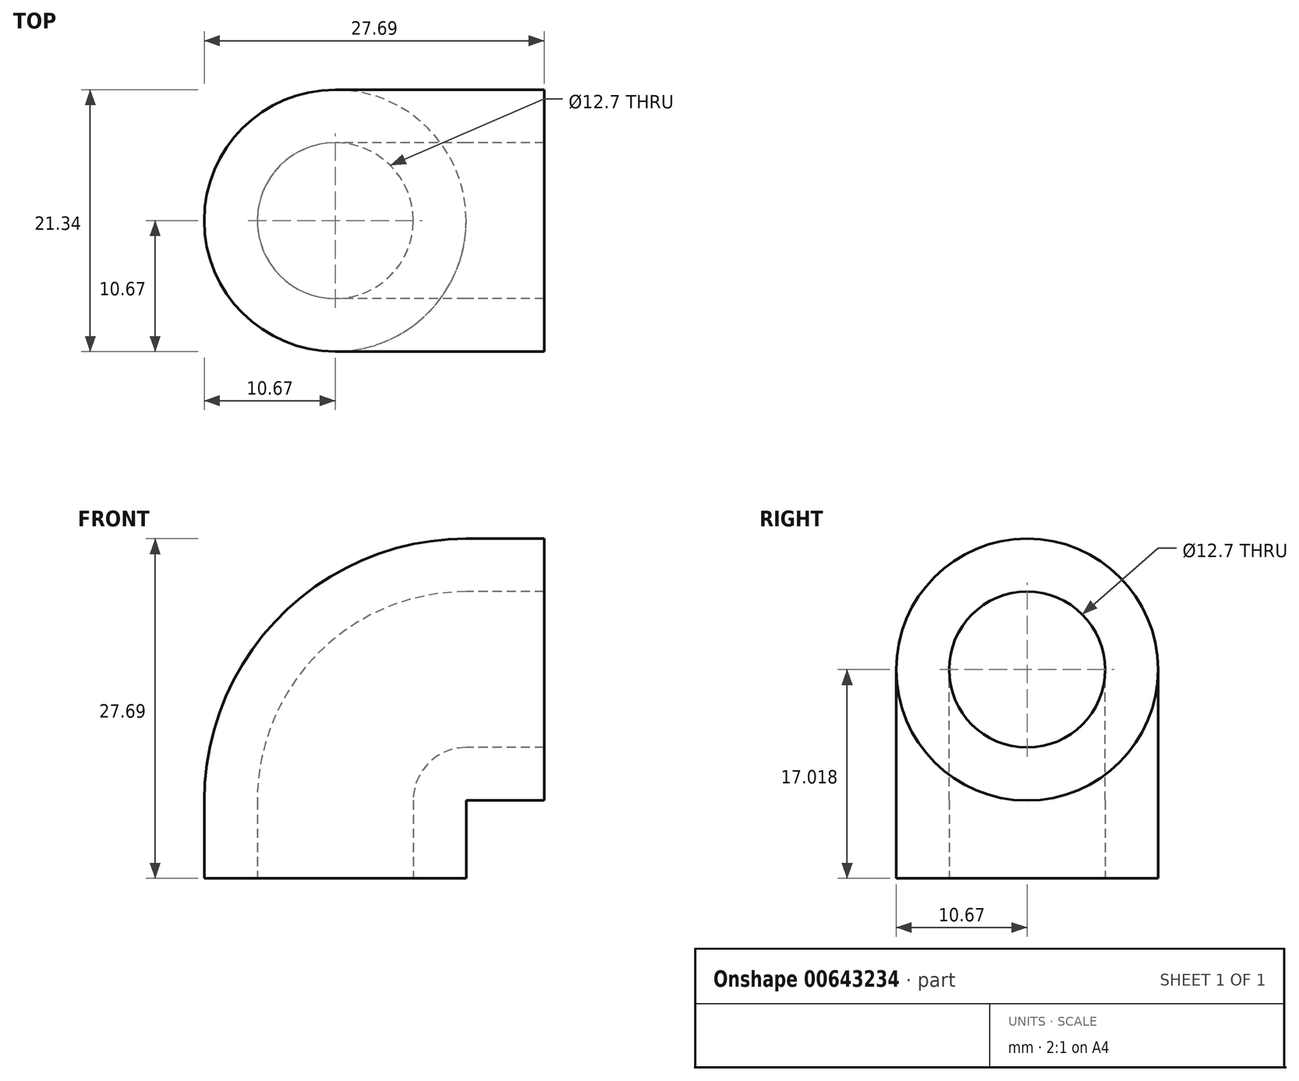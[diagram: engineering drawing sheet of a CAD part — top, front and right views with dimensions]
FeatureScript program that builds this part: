
annotation { "Feature Type Name" : "Feature", "Feature Type Description" : "" }
export const myFeature = defineFeature(function(context is Context, id is Id, definition is map)
    precondition{}
    {
        {
            var Q0;
            Q0=qCreatedBy(makeId("Top.planeOp"),FACE);
            var sketch = newSketch(context, id + "F0", { "sketchPlane" : qUnion([Q0])});
            skCircle(sketch, "E0", {"center": v(0, 0) * mm, "radius": 10.67 * mm});
            skCircle(sketch, "E1", {"center": v(0, 0) * mm, "radius": 6.35 * mm});
            skSolve(sketch);
        }
        {
            var Q0;
            Q0=makeQuery(id+"F0.imprint","IMPRINT",FACE,{"disambiguationData":[TD([[makeQuery(id+"F0.imprint","IMPRINT",EDGE,{"derivedFrom":sQuery(id+"F0.wireOp",EDGE,"E0")}),1.0]])]});
            extrude(context, id + "F1", {"entities" : qUnion([Q0]), "depth" : 6.35 * mm, "offsetDistance" : 25.4 * mm});
        }
        {
            var Q0;
            Q0=makeQuery(id+"F1.opExtrude","CAP_FACE",FACE,{"disambiguationData":[OSD([sQuery(id+"F0.wireOp",EDGE,"E0"),sQuery(id+"F0.wireOp",EDGE,"E1")])],"isStart":false});
            var sketch = newSketch(context, id + "F2", { "sketchPlane" : qUnion([Q0])});
            skLineSegment(sketch, "E2", {"start": v(10.67, 0) * mm, "end": v(10.67, 5.77) * mm});
            skLineSegment(sketch, "E3", {"start": v(10.67, 5.77) * mm, "end": v(10.67, -5.32) * mm});
            skSolve(sketch);
        }
        {
            var Q0;
            Q0=makeQuery(id+"F2.imprint","IMPRINT",FACE,{"disambiguationData":[TD([[makeQuery(id+"F2.imprint","IMPRINT",EDGE,{"derivedFrom":makeQuery(id+"F1.opExtrude","CAP_EDGE",EDGE,{"disambiguationData":[OSD([sQuery(id+"F0.wireOp",EDGE,"E0")])],"isStart":false})}),1.0]])]});
            var Q1;
            Q1=sQuery(id+"F2.wireOp",EDGE,"E3");
            revolve(context, id + "F3", {"operationType" : NewBodyOperationType.ADD, "entities" : qUnion([Q0]), "axis" : qUnion([Q1]), "revolveType" : RevolveType.ONE_DIRECTION, "oppositeDirection" : true, "angle" : 90 * degree});
        }
        {
            var Q0;
            Q0=makeQuery(id+"F3.opRevolve","CAP_FACE",FACE,{"disambiguationData":[OSD([sQuery(id+"F0.wireOp",EDGE,"E0"),sQuery(id+"F0.wireOp",EDGE,"E1")])],"isStart":false});
            var sketch = newSketch(context, id + "F4", { "sketchPlane" : qUnion([Q0])});
            skCircle(sketch, "E4", {"center": v(0, 17.02) * mm, "radius": 10.67 * mm});
            skCircle(sketch, "E5", {"center": v(0, 17.02) * mm, "radius": 6.35 * mm});
            skSolve(sketch);
        }
        {
            var Q0;
            Q0=makeQuery(id+"F4.imprint","IMPRINT",FACE,{"disambiguationData":[TD([[makeQuery(id+"F4.imprint","IMPRINT",EDGE,{"derivedFrom":sQuery(id+"F4.wireOp",EDGE,"E4")}),1.0]])]});
            extrude(context, id + "F5", {"entities" : qUnion([Q0]), "operationType" : NewBodyOperationType.ADD, "depth" : 6.35 * mm, "offsetDistance" : 25.4 * mm});
        }
    });
